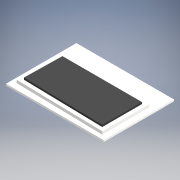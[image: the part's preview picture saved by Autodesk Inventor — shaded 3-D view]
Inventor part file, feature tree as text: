
AUTODESK INVENTOR PART (.ipt)
format: ipt  version: 2020 (Build 240168000, 168)  size: 255,488 bytes
history: native  units: mm
features: other x7, extrude x1, sketch x1
ambient origin geometry x8: Origin, YZ Plane, XZ Plane, XY Plane, X Axis, Y Axis, Z Axis, Center Point
bodies: Body1 (feature_tree), Body2 (feature_tree), Body3 (feature_tree), Body4 (feature_tree)
feature tree (9):
  other  "Твердое тело1"
  extrude  "Выдавливание1"  Depth=0.1mm TaperAngle=0.0deg
  other  "Твердое тело2"
  other  "Твердое тело3"
  sketch  "Эскиз2"
  other  "Твердое тело4"
  other  "pad"
  other  "glass1"
  other  "glass2"
